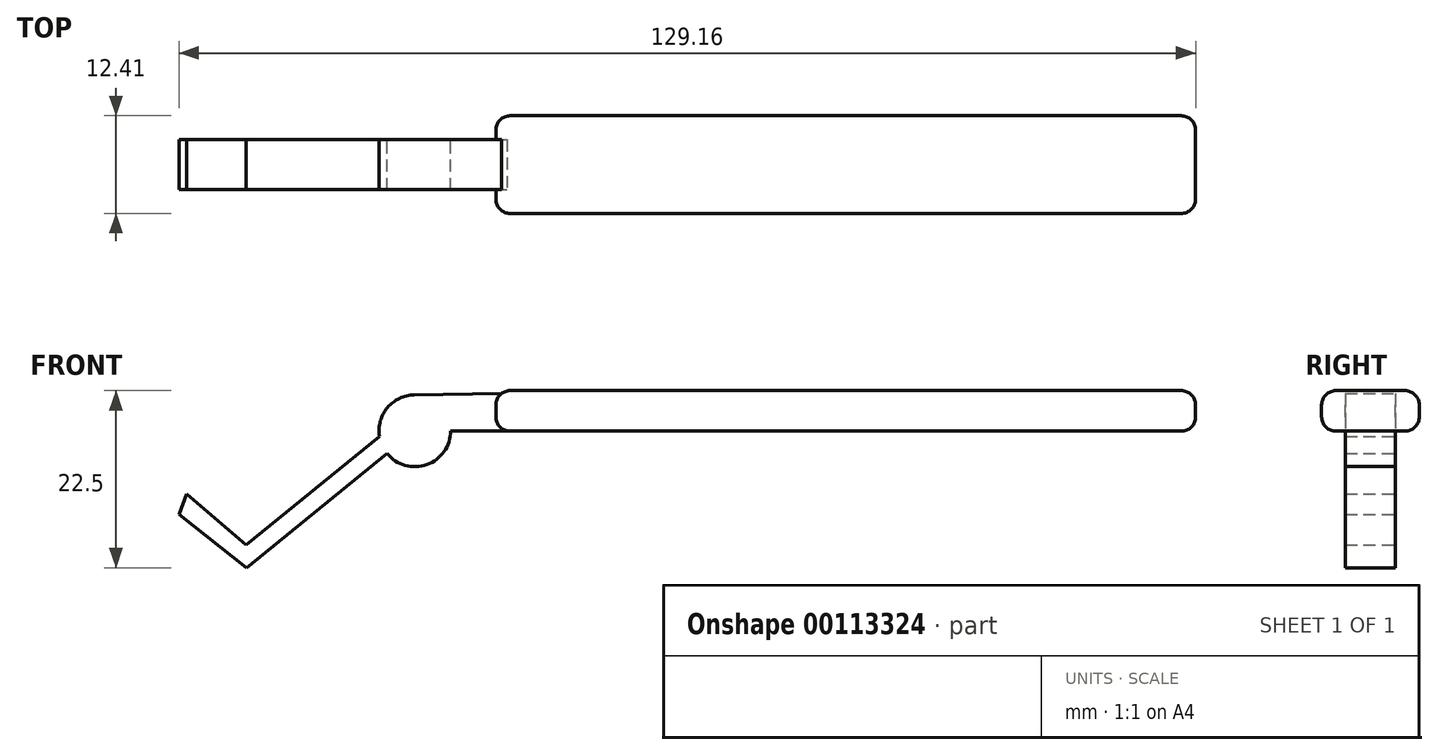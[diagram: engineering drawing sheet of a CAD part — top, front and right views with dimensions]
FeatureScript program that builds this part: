
annotation { "Feature Type Name" : "Feature", "Feature Type Description" : "" }
export const myFeature = defineFeature(function(context is Context, id is Id, definition is map)
    precondition{}
    {
        {
            var Q0;
            Q0=qCreatedBy(makeId("Front.planeOp"),FACE);
            var sketch = newSketch(context, id + "F0", { "sketchPlane" : qUnion([Q0])});
            skLineSegment(sketch, "E0", {"start": v(14.83, 24.83) * mm, "end": v(38.96, 24.83) * mm, "construction": true});
            skCircle(sketch, "E1", {"center": v(14.83, 24.83) * mm, "radius": 3.81 * mm, "construction": true});
            skCircle(sketch, "E2", {"center": v(38.96, 24.83) * mm, "radius": 3.81 * mm, "construction": true});
            skLineSegment(sketch, "E3", {"start": v(14.83, 21.02) * mm, "end": v(38.96, 21.02) * mm, "construction": true});
            skLineSegment(sketch, "E4", {"start": v(38.96, 28.64) * mm, "end": v(14.83, 28.64) * mm, "construction": true});
            skCircle(sketch, "E5", {"center": v(36.65, 33.99) * mm, "radius": 4.56 * mm});
            skLineSegment(sketch, "E6", {"start": v(36.65, 33.99) * mm, "end": v(15.3, 16.6) * mm});
            skLineSegment(sketch, "E7", {"start": v(15.3, 16.6) * mm, "end": v(6.68, 23.35) * mm});
            skLineSegment(sketch, "E8", {"start": v(7.65, 25.95) * mm, "end": v(15.2, 19.5) * mm});
            skLineSegment(sketch, "E9", {"start": v(15.2, 19.5) * mm, "end": v(32.15, 33.3) * mm});
            skLineSegment(sketch, "E10", {"start": v(7.65, 25.95) * mm, "end": v(6.68, 23.35) * mm});
            skLineSegment(sketch, "E11", {"start": v(36.65, 33.99) * mm, "end": v(72.34, 33.99) * mm});
            skLineSegment(sketch, "E12", {"start": v(72.34, 33.99) * mm, "end": v(72.34, 39.1) * mm});
            skLineSegment(sketch, "E13", {"start": v(72.34, 39.1) * mm, "end": v(36.58, 38.55) * mm});
            skSolve(sketch);
        }
        {
            var Q0;
            {var subQ7=sQuery(id+"F0.wireOp",EDGE,"an62Xjg7-xs1e-801o-4J7i-tVXNMO8gq07y");Q0=makeQuery(id+"F0.imprint","IMPRINT",FACE,{"disambiguationData":[TD([[makeQuery(id+"F0.imprint","IMPRINT",EDGE,{"derivedFrom":subQ7}),1.0]])]});}
            var Q1;
            {var subQ0=sQuery(id+"F0.wireOp",EDGE,"ZDsZ1z9R-bY8O-pkCL-OhkM-8RIaMmtdxEmm");var subQ1=makeQuery(id+"F0.imprint","INTERSECT",VERTEX,{"derivedFrom":[subQ0,sQuery(id+"F0.wireOp",EDGE,"PIOQilJV-1L53-h3SG-qBsx-qSoMfwHWGb4X")]});Q1=makeQuery(id+"F0.imprint","IMPRINT",FACE,{"disambiguationData":[TD([[makeQuery(id+"F0.imprint","IMPRINT",EDGE,{"disambiguationData":[TD([[subQ1,1.0]])],"derivedFrom":subQ0}),1.0]])]});}
            var Q2;
            {var subQ0=sQuery(id+"F0.wireOp",EDGE,"I6B12Tz3-ec6J-IiA4-sfc8-q1DKbHCQlqrA");Q2=makeQuery(id+"F0.imprint","IMPRINT",FACE,{"disambiguationData":[TD([[makeQuery(id+"F0.imprint","IMPRINT",EDGE,{"derivedFrom":subQ0}),1.0]])]});}
            var Q3;
            Q3=makeQuery(id+"F0.imprint","IMPRINT",FACE,{"disambiguationData":[TD([[makeQuery(id+"F0.imprint","IMPRINT",EDGE,{"derivedFrom":sQuery(id+"F0.wireOp",EDGE,"WteMS5BJ-g3WS-qfp8-aVoX-5HGdvGbBdg9W")}),1.0]])]});
            var Q4;
            {var subQ0=sQuery(id+"F0.wireOp",EDGE,"E5");var subQ1=makeQuery(id+"F0.imprint","INTERSECT",VERTEX,{"derivedFrom":[subQ0,sQuery(id+"F0.wireOp",EDGE,"cbTTmMgg-RBd7-ILVD-uh0W-Ob31dHpmlFub")]});Q4=makeQuery(id+"F0.imprint","IMPRINT",FACE,{"disambiguationData":[TD([[makeQuery(id+"F0.imprint","IMPRINT",EDGE,{"disambiguationData":[TD([[subQ1,1.0]])],"derivedFrom":subQ0}),1.0]])]});}
            var Q5;
            {var subQ0=sQuery(id+"F0.wireOp",EDGE,"m5GGaYTD-vsSV-aaW4-APL5-tRa7Izbm0CiF");Q5=makeQuery(id+"F0.imprint","IMPRINT",FACE,{"disambiguationData":[TD([[makeQuery(id+"F0.imprint","IMPRINT",EDGE,{"derivedFrom":subQ0}),-1.0]])]});}
            var Q6;
            {var subQ0=sQuery(id+"F0.wireOp",EDGE,"Uu1b8pSS-dsNJ-1Wvz-XI3k-GBjDiCiDkx1b");Q6=makeQuery(id+"F0.imprint","IMPRINT",FACE,{"disambiguationData":[TD([[makeQuery(id+"F0.imprint","IMPRINT",EDGE,{"derivedFrom":subQ0}),1.0]])]});}
            var Q7;
            {var subQ0=sQuery(id+"F0.wireOp",EDGE,"SR9jicmi-Y4Vd-m0Fm-LlZf-eTBj7cfcOfBr");Q7=makeQuery(id+"F0.imprint","IMPRINT",FACE,{"disambiguationData":[TD([[makeQuery(id+"F0.imprint","IMPRINT",EDGE,{"derivedFrom":subQ0}),1.0]])]});}
            var Q8;
            {var subQ0=sQuery(id+"F0.wireOp",EDGE,"E7");Q8=makeQuery(id+"F0.imprint","IMPRINT",FACE,{"disambiguationData":[TD([[makeQuery(id+"F0.imprint","IMPRINT",EDGE,{"derivedFrom":subQ0}),-1.0]])]});}
            var Q9;
            {var subQ0=sQuery(id+"F0.wireOp",EDGE,"E11");var subQ1=sQuery(id+"F0.wireOp",EDGE,"E5");var subQ2=makeQuery(id+"F0.imprint","INTERSECT",VERTEX,{"derivedFrom":[subQ1,subQ0]});Q9=makeQuery(id+"F0.imprint","IMPRINT",FACE,{"disambiguationData":[TD([[makeQuery(id+"F0.imprint","IMPRINT",EDGE,{"disambiguationData":[TD([[subQ2,1.0]])],"derivedFrom":subQ1}),1.0]])]});}
            var Q10;
            {var subQ4=sQuery(id+"F0.wireOp",EDGE,"E12");Q10=makeQuery(id+"F0.imprint","IMPRINT",FACE,{"disambiguationData":[TD([[makeQuery(id+"F0.imprint","IMPRINT",EDGE,{"derivedFrom":subQ4}),1.0]])]});}
            extrude(context, id + "F1", {"entities" : qUnion([Q0, Q1, Q2, Q3, Q4, Q5, Q6, Q7, Q8, Q9, Q10]), "depth" : 6.35 * mm});
        }
        {
            var Q0;
            Q0=makeQuery(id+"F1.opExtrude","SWEPT_FACE",FACE,{"disambiguationData":[OSD([sQuery(id+"F0.wireOp",EDGE,"E12")])]});
            var sketch = newSketch(context, id + "F2", { "sketchPlane" : qUnion([Q0])});
            skLineSegment(sketch, "E14", {"start": v(-6.35, 39.1) * mm, "end": v(-9.38, 39.1) * mm});
            skLineSegment(sketch, "E15", {"start": v(-9.38, 39.1) * mm, "end": v(-9.38, 33.94) * mm});
            skLineSegment(sketch, "E16", {"start": v(-9.38, 33.94) * mm, "end": v(3.03, 33.94) * mm});
            skLineSegment(sketch, "E17", {"start": v(3.03, 33.94) * mm, "end": v(3.03, 39.1) * mm});
            skLineSegment(sketch, "E18", {"start": v(3.03, 39.1) * mm, "end": v(0, 39.1) * mm});
            skSolve(sketch);
        }
        {
            var Q0;
            {var subQ0=sQuery(id+"F0.wireOp",EDGE,"E12");Q0=makeQuery(id+"F2.imprint","IMPRINT",FACE,{"disambiguationData":[TD([[makeQuery(id+"F2.imprint","IMPRINT",EDGE,{"derivedFrom":makeQuery(id+"F1.opExtrude","CAP_EDGE",EDGE,{"disambiguationData":[OSD([subQ0])],"isStart":true})}),1.0]])]});}
            var Q1;
            Q1=makeQuery(id+"F2.imprint","IMPRINT",FACE,{"disambiguationData":[TD([[makeQuery(id+"F2.imprint","IMPRINT",EDGE,{"derivedFrom":sQuery(id+"F2.wireOp",EDGE,"E14")}),1.0]])]});
            extrude(context, id + "F3", {"entities" : qUnion([Q0, Q1]), "operationType" : NewBodyOperationType.ADD, "oppositeDirection" : true, "depth" : 25.4 * mm});
        }
        {
            var Q0;
            {var subQ0=sQuery(id+"F0.wireOp",EDGE,"E12");Q0=makeQuery(id+"F3.boolean.opBoolean","MERGE",FACE,{"derivedFrom":[makeQuery(id+"F1.opExtrude","SWEPT_FACE",FACE,{"disambiguationData":[OSD([subQ0])]}),makeQuery(id+"F3.opExtrude","CAP_FACE",FACE,{"disambiguationData":[OSD([subQ0,sQuery(id+"F0.wireOp",EDGE,"E13"),sQuery(id+"F2.wireOp",EDGE,"E14"),sQuery(id+"F2.wireOp",EDGE,"E15"),sQuery(id+"F2.wireOp",EDGE,"E16"),sQuery(id+"F2.wireOp",EDGE,"E17"),sQuery(id+"F2.wireOp",EDGE,"E18")])],"isStart":true})]});}
            extrude(context, id + "F4", {"entities" : qUnion([Q0]), "operationType" : NewBodyOperationType.ADD, "depth" : 63.5 * mm});
        }
        {
            var Q0;
            {var subQ0=sQuery(id+"F2.wireOp",EDGE,"E15");var subQ1=sQuery(id+"F2.wireOp",EDGE,"E14");Q0=makeQuery(id+"F4.boolean.opBoolean","MERGE",EDGE,{"derivedFrom":[makeQuery(id+"F3.opExtrude","SWEPT_EDGE",EDGE,{"disambiguationData":[OSD([subQ1,subQ0])]}),makeQuery(id+"F4.opExtrude","SWEPT_EDGE",EDGE,{"disambiguationData":[OSD([subQ1,subQ0])]})]});}
            var Q1;
            Q1=makeQuery(id+"F3.opExtrude","CAP_EDGE",EDGE,{"disambiguationData":[OSD([sQuery(id+"F2.wireOp",EDGE,"E15")])],"isStart":false});
            var Q2;
            {var subQ0=sQuery(id+"F2.wireOp",EDGE,"E16");var subQ1=sQuery(id+"F2.wireOp",EDGE,"E15");Q2=makeQuery(id+"F4.boolean.opBoolean","MERGE",EDGE,{"derivedFrom":[makeQuery(id+"F3.opExtrude","SWEPT_EDGE",EDGE,{"disambiguationData":[OSD([subQ1,subQ0])]}),makeQuery(id+"F4.opExtrude","SWEPT_EDGE",EDGE,{"disambiguationData":[OSD([subQ1,subQ0])]})]});}
            var Q3;
            Q3=makeQuery(id+"F3.opExtrude","CAP_EDGE",EDGE,{"disambiguationData":[OSD([sQuery(id+"F0.wireOp",EDGE,"E12"),sQuery(id+"F0.wireOp",EDGE,"E13"),sQuery(id+"F2.wireOp",EDGE,"E14"),sQuery(id+"F2.wireOp",EDGE,"E18")])],"isStart":false});
            var Q4;
            Q4=makeQuery(id+"F3.opExtrude","CAP_EDGE",EDGE,{"disambiguationData":[OSD([sQuery(id+"F2.wireOp",EDGE,"E16")])],"isStart":false});
            var Q5;
            Q5=makeQuery(id+"F3.opExtrude","CAP_EDGE",EDGE,{"disambiguationData":[OSD([sQuery(id+"F2.wireOp",EDGE,"E17")])],"isStart":false});
            var Q6;
            {var subQ0=sQuery(id+"F2.wireOp",EDGE,"E18");var subQ1=sQuery(id+"F2.wireOp",EDGE,"E17");Q6=makeQuery(id+"F4.boolean.opBoolean","MERGE",EDGE,{"derivedFrom":[makeQuery(id+"F3.opExtrude","SWEPT_EDGE",EDGE,{"disambiguationData":[OSD([subQ1,subQ0])]}),makeQuery(id+"F4.opExtrude","SWEPT_EDGE",EDGE,{"disambiguationData":[OSD([subQ1,subQ0])]})]});}
            var Q7;
            Q7=makeQuery(id+"F4.opExtrude","CAP_EDGE",EDGE,{"disambiguationData":[OSD([sQuery(id+"F2.wireOp",EDGE,"E15")])],"isStart":false});
            var Q8;
            Q8=makeQuery(id+"F4.opExtrude","CAP_EDGE",EDGE,{"disambiguationData":[OSD([sQuery(id+"F0.wireOp",EDGE,"E12"),sQuery(id+"F0.wireOp",EDGE,"E13"),sQuery(id+"F2.wireOp",EDGE,"E14"),sQuery(id+"F2.wireOp",EDGE,"E18")])],"isStart":false});
            var Q9;
            Q9=makeQuery(id+"F4.opExtrude","CAP_EDGE",EDGE,{"disambiguationData":[OSD([sQuery(id+"F2.wireOp",EDGE,"E17")])],"isStart":false});
            var Q10;
            Q10=makeQuery(id+"F4.opExtrude","CAP_EDGE",EDGE,{"disambiguationData":[OSD([sQuery(id+"F2.wireOp",EDGE,"E16")])],"isStart":false});
            var Q11;
            {var subQ0=sQuery(id+"F2.wireOp",EDGE,"E17");var subQ1=sQuery(id+"F2.wireOp",EDGE,"E16");Q11=makeQuery(id+"F4.boolean.opBoolean","MERGE",EDGE,{"derivedFrom":[makeQuery(id+"F3.opExtrude","SWEPT_EDGE",EDGE,{"disambiguationData":[OSD([subQ1,subQ0])]}),makeQuery(id+"F4.opExtrude","SWEPT_EDGE",EDGE,{"disambiguationData":[OSD([subQ1,subQ0])]})]});}
            fillet(context, id + "F5", {"entities" : qUnion([Q0, Q1, Q2, Q3, Q4, Q5, Q6, Q7, Q8, Q9, Q10, Q11]), "radius" : 1.84 * mm, "tangentPropagation" : true, "allowEdgeOverflow" : false});
        }
    });
